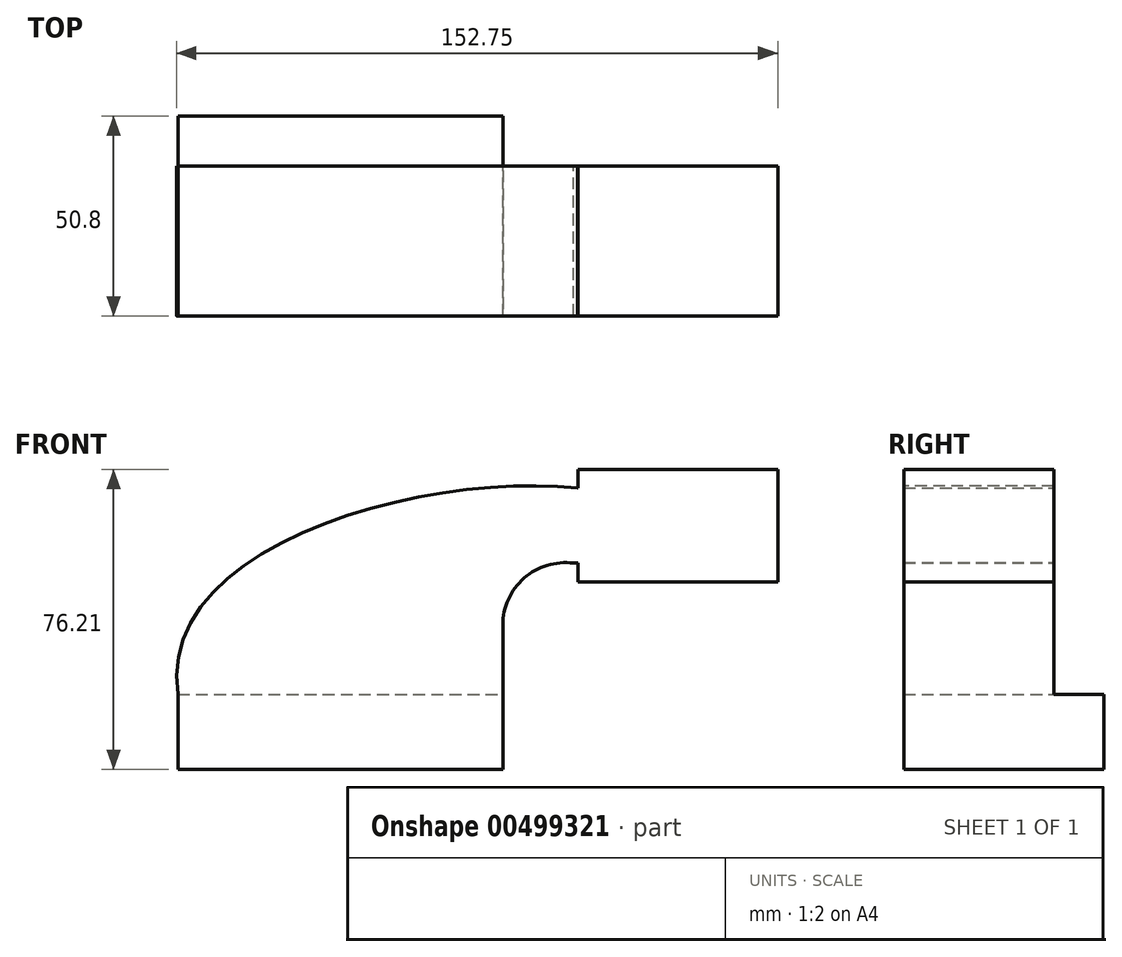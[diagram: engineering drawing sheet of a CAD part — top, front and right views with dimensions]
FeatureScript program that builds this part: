
annotation { "Feature Type Name" : "Feature", "Feature Type Description" : "" }
export const myFeature = defineFeature(function(context is Context, id is Id, definition is map)
    precondition{}
    {
        {
            var Q0;
            Q0=qCreatedBy(makeId("Front.planeOp"),FACE);
            var sketch = newSketch(context, id + "F0", { "sketchPlane" : qUnion([Q0])});
            skLineSegment(sketch, "E0.bottom", {"start": v(37.77, -9.53) * mm, "end": v(-44.78, -9.52) * mm});
            skLineSegment(sketch, "E0.top", {"start": v(37.77, 9.52) * mm, "end": v(-44.78, 9.53) * mm});
            skLineSegment(sketch, "E0.left", {"start": v(37.77, -9.52) * mm, "end": v(37.77, 9.52) * mm});
            skLineSegment(sketch, "E0.right", {"start": v(-44.78, -9.52) * mm, "end": v(-44.78, 9.52) * mm});
            skPoint(sketch, "E0.middle", {"position": v(-3.5, 0) * mm});
            skLineSegment(sketch, "E1.bottom", {"start": v(107.62, 38.1) * mm, "end": v(56.82, 38.1) * mm});
            skLineSegment(sketch, "E1.top", {"start": v(107.62, 66.68) * mm, "end": v(56.82, 66.68) * mm});
            skLineSegment(sketch, "E1.left", {"start": v(107.62, 38.1) * mm, "end": v(107.62, 66.67) * mm});
            skLineSegment(sketch, "E1.right", {"start": v(56.82, 38.1) * mm, "end": v(56.82, 66.67) * mm});
            skPoint(sketch, "E1.middle", {"position": v(82.22, 52.39) * mm});
            skLineSegment(sketch, "E2", {"start": v(37.77, 9.52) * mm, "end": v(37.77, 27.14) * mm});
            skArc(sketch, "E3", {"start": v(37.77, 27.14) * mm, "mid": v(43.18, 39.07) * mm, "end": v(55.72, 42.88) * mm});
            skLineSegment(sketch, "E4", {"start": v(55.72, 42.88) * mm, "end": v(87.47, 42.88) * mm});
            skLineSegment(sketch, "E5.0", {"start": v(56.73, 61.93) * mm, "end": v(87.47, 61.93) * mm});
            skArc(sketch, "E5.1", {"start": v(18.72, 27.14) * mm, "mid": v(30.07, 52.9) * mm, "end": v(56.73, 61.93) * mm});
            skLineSegment(sketch, "E5.2", {"start": v(18.72, 9.52) * mm, "end": v(18.72, 27.14) * mm});
            skLineSegment(sketch, "E6", {"start": v(87.47, 61.93) * mm, "end": v(87.47, 38.1) * mm});
            skFitSpline(sketch, "E7", {"points": [v(-44.78, 9.52) * mm, v(56.73, 61.93) * mm], "startDerivative": vector(-17.51, 115.27) * mm, "endDerivative": vector(113.94, -12.97) * mm});
            skSolve(sketch);
        }
        {
            var Q0;
            Q0=makeQuery(id+"F0.imprint","IMPRINT",FACE,{"disambiguationData":[TD([[makeQuery(id+"F0.imprint","IMPRINT",EDGE,{"derivedFrom":sQuery(id+"F0.wireOp",EDGE,"E0.bottom")}),-1.0]])]});
            extrude(context, id + "F1", {"entities" : qUnion([Q0]), "oppositeDirection" : true, "depth" : 25.4 * mm});
        }
        {
            var Q0;
            Q0 = qSketchRegion(id + "F0", true);
            extrude(context, id + "F2", {"entities" : qUnion([Q0]), "operationType" : NewBodyOperationType.ADD, "endBound" : BoundingType.SYMMETRIC, "depth" : 25.4 * mm});
        }
        {
            var Q0;
            Q0 = qSketchRegion(id + "F0", true);
            extrude(context, id + "F3", {"entities" : qUnion([Q0]), "operationType" : NewBodyOperationType.ADD, "depth" : 25.4 * mm});
        }
    });
